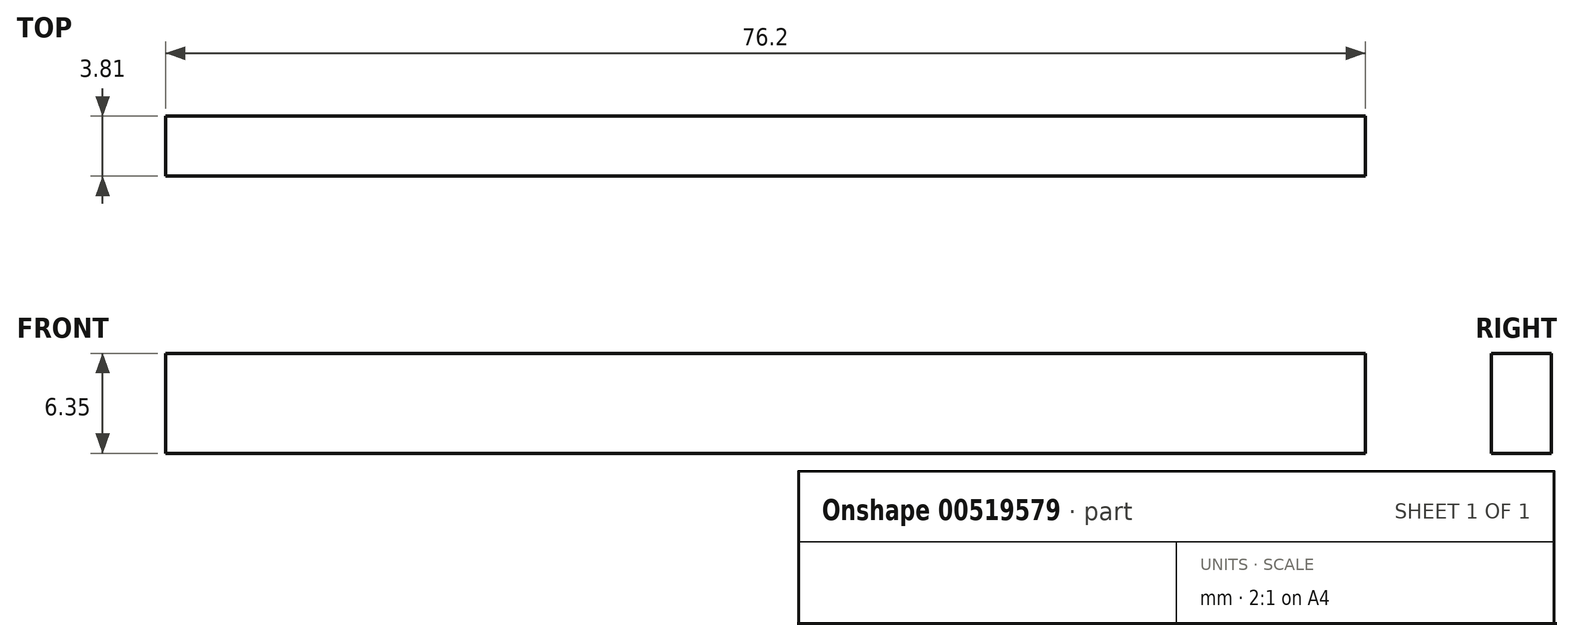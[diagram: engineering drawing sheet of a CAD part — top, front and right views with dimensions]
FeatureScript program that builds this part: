
annotation { "Feature Type Name" : "Feature", "Feature Type Description" : "" }
export const myFeature = defineFeature(function(context is Context, id is Id, definition is map)
    precondition{}
    {
        {
            var Q0;
            Q0=qCreatedBy(makeId("Front.planeOp"),FACE);
            var sketch = newSketch(context, id + "F0", { "sketchPlane" : qUnion([Q0])});
            skLineSegment(sketch, "E0.bottom", {"start": v(-43.16, 15.3) * mm, "end": v(33.04, 15.3) * mm});
            skLineSegment(sketch, "E0.top", {"start": v(-43.16, 8.94) * mm, "end": v(33.04, 8.94) * mm});
            skLineSegment(sketch, "E0.left", {"start": v(-43.16, 15.3) * mm, "end": v(-43.16, 8.94) * mm});
            skLineSegment(sketch, "E0.right", {"start": v(33.04, 15.3) * mm, "end": v(33.04, 8.94) * mm});
            skSolve(sketch);
        }
        {
            var Q0;
            Q0 = qSketchRegion(id + "F0", true);
            extrude(context, id + "F1", {"entities" : qUnion([Q0]), "oppositeDirection" : true, "depth" : 3.8 * mm, "offsetDistance" : 25.4 * mm});
        }
    });
